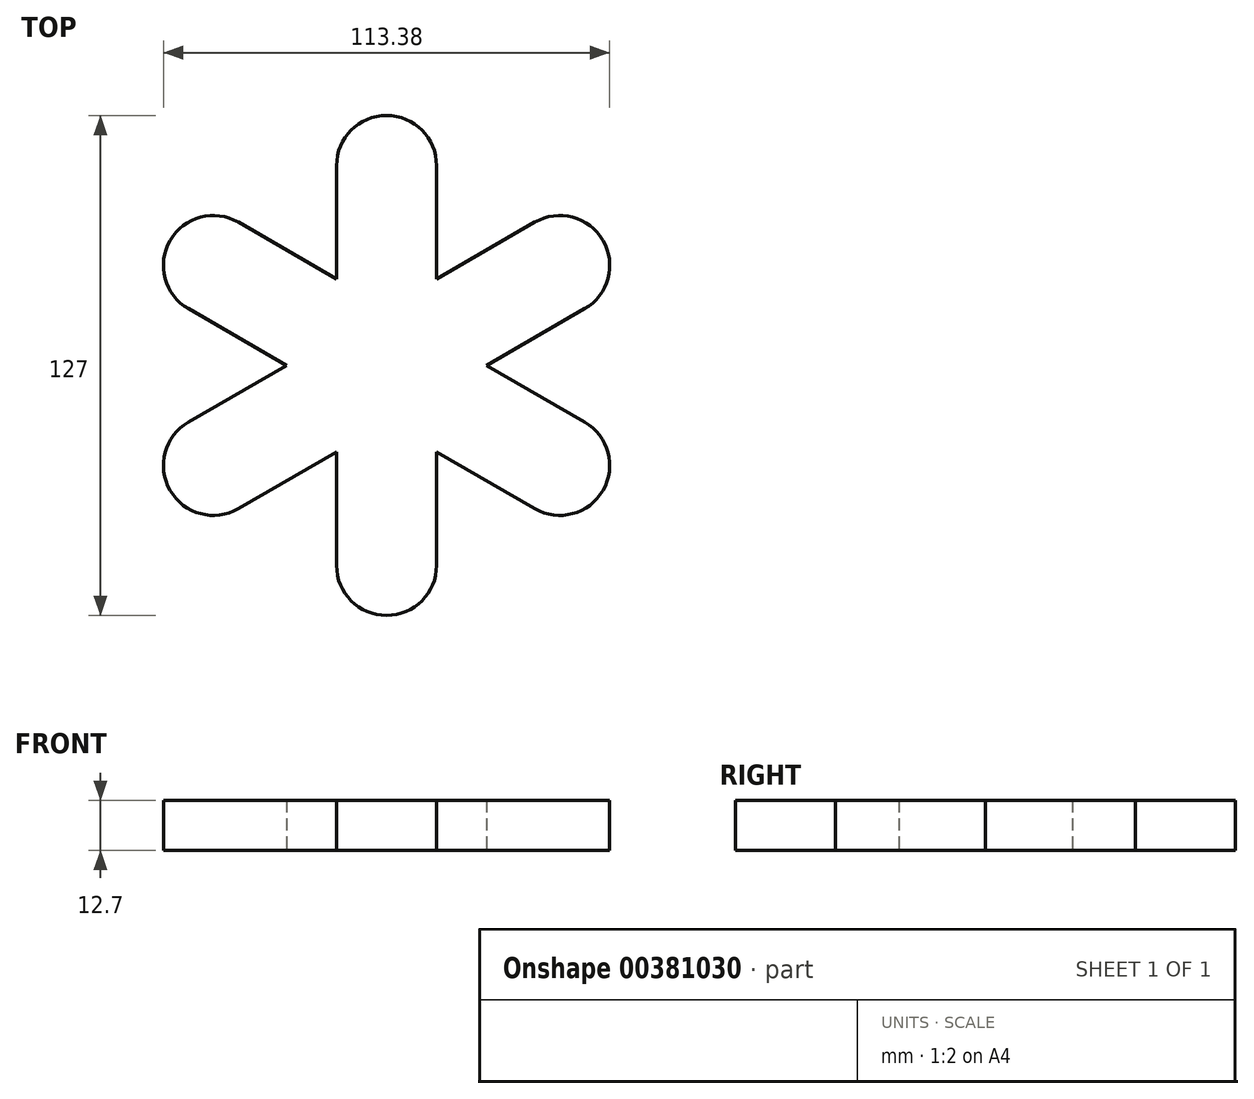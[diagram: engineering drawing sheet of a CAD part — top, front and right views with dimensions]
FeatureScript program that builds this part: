
annotation { "Feature Type Name" : "Feature", "Feature Type Description" : "" }
export const myFeature = defineFeature(function(context is Context, id is Id, definition is map)
    precondition{}
    {
        {
            var Q0;
            Q0=qCreatedBy(makeId("Top.planeOp"),FACE);
            var sketch = newSketch(context, id + "F0", { "sketchPlane" : qUnion([Q0])});
            skArc(sketch, "E0", {"start": v(12.7, 50.8) * mm, "mid": v(0, 63.5) * mm, "end": v(-12.7, 50.8) * mm});
            skArc(sketch, "E1.1.0", {"start": v(-37.64, 36.4) * mm, "mid": v(-55, 31.75) * mm, "end": v(-50.34, 14.4) * mm});
            skLineSegment(sketch, "E1.1.1", {"start": v(-25.4, 0) * mm, "end": v(-50.34, 14.4) * mm});
            skArc(sketch, "E1.2.0", {"start": v(-50.34, -14.4) * mm, "mid": v(-55, -31.75) * mm, "end": v(-37.64, -36.4) * mm});
            skPoint(sketch, "E1.center", {"position": v(0, 0) * mm});
            skArc(sketch, "E2.3.3.0", {"start": v(-12.7, -50.8) * mm, "mid": v(0, -63.5) * mm, "end": v(12.7, -50.8) * mm});
            skArc(sketch, "E2.3.4.0", {"start": v(37.64, -36.4) * mm, "mid": v(55, -31.75) * mm, "end": v(50.34, -14.4) * mm});
            skArc(sketch, "E2.3.5.0", {"start": v(50.34, 14.4) * mm, "mid": v(55, 31.75) * mm, "end": v(37.64, 36.4) * mm});
            skLineSegment(sketch, "E3.trimOffspring", {"start": v(-12.7, 22) * mm, "end": v(-37.64, 36.4) * mm});
            skLineSegment(sketch, "E4.trimOffspring", {"start": v(12.7, 22) * mm, "end": v(37.64, 36.4) * mm});
            skLineSegment(sketch, "E5.trimOffspring", {"start": v(12.7, 22) * mm, "end": v(12.7, 50.8) * mm});
            skLineSegment(sketch, "E6.trimOffspring", {"start": v(25.4, 0) * mm, "end": v(50.34, -14.4) * mm});
            skLineSegment(sketch, "E7.trimOffspring", {"start": v(25.4, 0) * mm, "end": v(50.34, 14.4) * mm});
            skLineSegment(sketch, "E8.trimOffspring", {"start": v(12.7, -22) * mm, "end": v(12.7, -50.8) * mm});
            skLineSegment(sketch, "E9.trimOffspring", {"start": v(12.7, -22) * mm, "end": v(37.64, -36.4) * mm});
            skLineSegment(sketch, "E10.trimOffspring", {"start": v(-12.7, -22) * mm, "end": v(-37.64, -36.4) * mm});
            skLineSegment(sketch, "E11.trimOffspring", {"start": v(-12.7, -22) * mm, "end": v(-12.7, -50.8) * mm});
            skLineSegment(sketch, "E12.trimOffspring", {"start": v(-25.4, 0) * mm, "end": v(-50.34, -14.4) * mm});
            skLineSegment(sketch, "E13.trimOffspring", {"start": v(-12.7, 22) * mm, "end": v(-12.7, 50.8) * mm});
            skPoint(sketch, "E14.orphan", {"position": v(12.7, 0) * mm});
            skPoint(sketch, "E2.10.5.0.end.orphan", {"position": v(-12.7, 0) * mm});
            skSolve(sketch);
        }
        {
            var Q0;
            Q0 = qSketchRegion(id + "F0", true);
            extrude(context, id + "F1", {"entities" : qUnion([Q0]), "depth" : 12.7 * mm});
        }
    });
